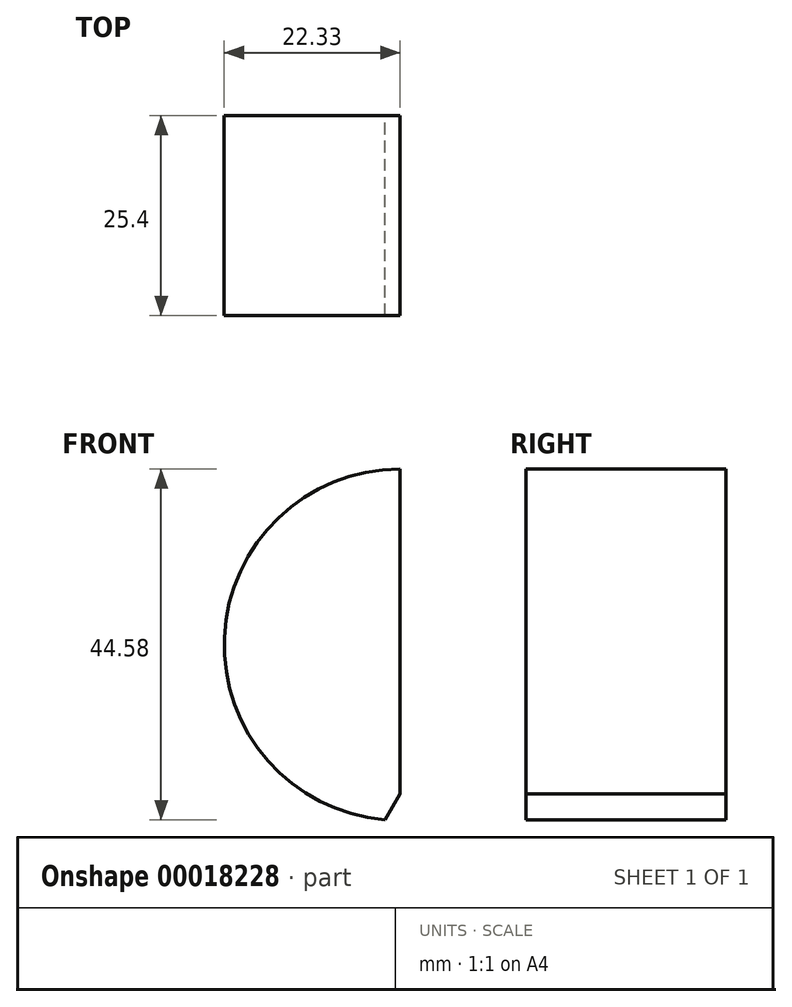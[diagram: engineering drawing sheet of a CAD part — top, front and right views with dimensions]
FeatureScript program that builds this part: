
annotation { "Feature Type Name" : "Feature", "Feature Type Description" : "" }
export const myFeature = defineFeature(function(context is Context, id is Id, definition is map)
    precondition{}
    {
        {
            var Q0;
            Q0=qCreatedBy(makeId("Front.planeOp"),FACE);
            var sketch = newSketch(context, id + "F0", { "sketchPlane" : qUnion([Q0])});
            skLineSegment(sketch, "E0", {"start": v(0, 22.33) * mm, "end": v(0, -18.95) * mm});
            skLineSegment(sketch, "E1", {"start": v(-1.9, -22.25) * mm, "end": v(0, -18.95) * mm});
            skArc(sketch, "E2", {"start": v(0, 22.33) * mm, "mid": v(-22.3, 0.95) * mm, "end": v(-1.9, -22.25) * mm});
            skSolve(sketch);
        }
        {
            var Q0;
            Q0=makeQuery(id+"F0.imprint","IMPRINT",FACE,{"disambiguationData":[TD([[makeQuery(id+"F0.imprint","IMPRINT",EDGE,{"derivedFrom":sQuery(id+"F0.wireOp",EDGE,"E0")}),-1.0]])]});
            extrude(context, id + "F1", {"entities" : qUnion([Q0]), "depth" : 25.4 * mm});
        }
    });
